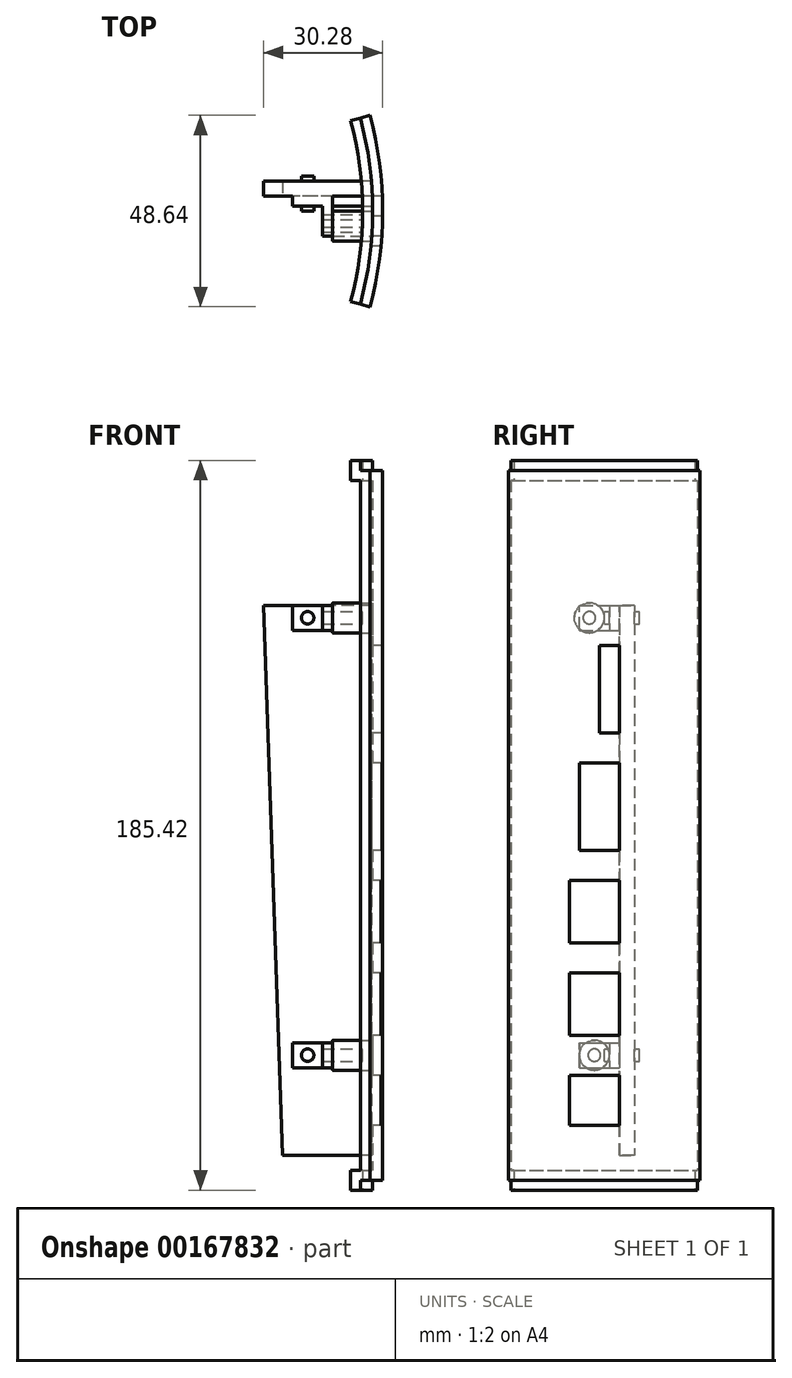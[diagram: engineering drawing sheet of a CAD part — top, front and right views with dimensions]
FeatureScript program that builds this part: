
annotation { "Feature Type Name" : "Feature", "Feature Type Description" : "" }
export const myFeature = defineFeature(function(context is Context, id is Id, definition is map)
    precondition{}
    {
        {
            var Q0;
            Q0=qCreatedBy(makeId("Front.planeOp"),FACE);
            var sketch = newSketch(context, id + "F0", { "sketchPlane" : qUnion([Q0])});
            skLineSegment(sketch, "E0.bottom", {"start": v(0, 146.05) * mm, "end": v(-27.74, 146.05) * mm});
            skLineSegment(sketch, "E0.top", {"start": v(0, 6.35) * mm, "end": v(-22.86, 6.35) * mm});
            skLineSegment(sketch, "E0.left", {"start": v(0, 146.05) * mm, "end": v(0, 6.35) * mm});
            skPoint(sketch, "E0.middle", {"position": v(0, 0) * mm});
            skLineSegment(sketch, "E1.top", {"start": v(2.54, 113.67) * mm, "end": v(-22.86, 113.67) * mm});
            skLineSegment(sketch, "E1.left", {"start": v(2.54, 135.89) * mm, "end": v(2.54, 113.66) * mm});
            skLineSegment(sketch, "E1.right", {"start": v(-22.86, 135.89) * mm, "end": v(-22.86, 113.66) * mm});
            skLineSegment(sketch, "E2.bottom", {"start": v(2.54, 106.05) * mm, "end": v(-19.69, 106.05) * mm});
            skLineSegment(sketch, "E2.top", {"start": v(2.54, 83.82) * mm, "end": v(-19.69, 83.82) * mm});
            skLineSegment(sketch, "E2.left", {"start": v(2.54, 106.04) * mm, "end": v(2.54, 83.82) * mm});
            skLineSegment(sketch, "E2.right", {"start": v(-19.69, 106.04) * mm, "end": v(-19.69, 83.82) * mm});
            skLineSegment(sketch, "E3.bottom", {"start": v(2.54, 76.2) * mm, "end": v(-15.88, 76.2) * mm});
            skLineSegment(sketch, "E3.top", {"start": v(2.54, 60.32) * mm, "end": v(-15.88, 60.32) * mm});
            skLineSegment(sketch, "E3.left", {"start": v(2.54, 76.2) * mm, "end": v(2.54, 60.32) * mm});
            skLineSegment(sketch, "E3.right", {"start": v(-15.88, 76.2) * mm, "end": v(-15.88, 60.32) * mm});
            skLineSegment(sketch, "E4.bottom", {"start": v(2.54, 52.7) * mm, "end": v(-13.34, 52.7) * mm});
            skLineSegment(sketch, "E4.top", {"start": v(2.54, 36.83) * mm, "end": v(-13.34, 36.83) * mm});
            skLineSegment(sketch, "E4.left", {"start": v(2.54, 52.7) * mm, "end": v(2.54, 36.83) * mm});
            skLineSegment(sketch, "E4.right", {"start": v(-13.34, 52.7) * mm, "end": v(-13.34, 36.83) * mm});
            skLineSegment(sketch, "E5.bottom", {"start": v(2.54, 26.67) * mm, "end": v(-16.51, 26.67) * mm});
            skLineSegment(sketch, "E5.top", {"start": v(2.54, 13.97) * mm, "end": v(-16.51, 13.97) * mm});
            skLineSegment(sketch, "E5.left", {"start": v(2.54, 26.67) * mm, "end": v(2.54, 13.97) * mm});
            skLineSegment(sketch, "E5.right", {"start": v(-16.51, 26.67) * mm, "end": v(-16.51, 13.97) * mm});
            skLineSegment(sketch, "E6", {"start": v(-22.86, 135.9) * mm, "end": v(2.54, 135.9) * mm});
            skLineSegment(sketch, "E7", {"start": v(-22.86, 6.35) * mm, "end": v(-27.74, 146.05) * mm});
            skLineSegment(sketch, "E8.bottom", {"start": v(-12.7, 139.7) * mm, "end": v(-20.32, 139.7) * mm});
            skLineSegment(sketch, "E8.top", {"start": v(-12.7, 146.05) * mm, "end": v(-22.86, 146.05) * mm});
            skLineSegment(sketch, "E8.left", {"start": v(-12.7, 139.7) * mm, "end": v(-12.7, 146.05) * mm});
            skLineSegment(sketch, "E9.bottom", {"start": v(-12.7, 28.57) * mm, "end": v(-20.32, 28.57) * mm});
            skLineSegment(sketch, "E9.top", {"start": v(-12.7, 34.92) * mm, "end": v(-20.32, 34.92) * mm});
            skLineSegment(sketch, "E9.left", {"start": v(-12.7, 28.57) * mm, "end": v(-12.7, 34.92) * mm});
            skLineSegment(sketch, "E10", {"start": v(-20.32, 34.92) * mm, "end": v(-20.32, 28.57) * mm});
            skLineSegment(sketch, "E11", {"start": v(-20.32, 146.05) * mm, "end": v(-20.32, 139.7) * mm});
            skCircle(sketch, "E12", {"center": v(-16.51, 31.75) * mm, "radius": 1.59 * mm});
            skCircle(sketch, "E13", {"center": v(-16.51, 142.87) * mm, "radius": 1.59 * mm});
            skPoint(sketch, "E14", {"position": v(0, 36.83) * mm});
            skPoint(sketch, "E15", {"position": v(0, 26.67) * mm});
            skPoint(sketch, "E16", {"position": v(0, 31.75) * mm});
            skLineSegment(sketch, "E17", {"start": v(0, 31.75) * mm, "end": v(-37.76, 31.75) * mm, "construction": true});
            skPoint(sketch, "E18", {"position": v(-12.7, 31.75) * mm});
            skPoint(sketch, "E19", {"position": v(-12.7, 142.87) * mm});
            skLineSegment(sketch, "E20", {"start": v(-2.37, 142.87) * mm, "end": v(-23.9, 142.87) * mm, "construction": true});
            skPoint(sketch, "E20.endSnap0", {"position": v(-22.86, 142.87) * mm});
            skLineSegment(sketch, "E21", {"start": v(-12.7, 139.7) * mm, "end": v(-10.16, 139.7) * mm});
            skLineSegment(sketch, "E22", {"start": v(-10.16, 139.7) * mm, "end": v(-10.16, 146.05) * mm});
            skLineSegment(sketch, "E23", {"start": v(-12.7, 34.92) * mm, "end": v(-10.16, 34.92) * mm});
            skLineSegment(sketch, "E24", {"start": v(-10.16, 34.92) * mm, "end": v(-10.16, 28.57) * mm});
            skLineSegment(sketch, "E25", {"start": v(-10.16, 28.57) * mm, "end": v(-12.7, 28.57) * mm});
            skSolve(sketch);
        }
        {
            var Q0;
            {var subQ5=sQuery(id+"F0.wireOp",EDGE,"E1.right");Q0=makeQuery(id+"F0.imprint","IMPRINT",FACE,{"disambiguationData":[TD([[makeQuery(id+"F0.imprint","IMPRINT",EDGE,{"derivedFrom":subQ5}),1.0]])]});}
            var Q1;
            {var subQ5=sQuery(id+"F0.wireOp",EDGE,"E4.right");Q1=makeQuery(id+"F0.imprint","IMPRINT",FACE,{"disambiguationData":[TD([[makeQuery(id+"F0.imprint","IMPRINT",EDGE,{"derivedFrom":subQ5}),1.0]])]});}
            var Q2;
            {var subQ5=sQuery(id+"F0.wireOp",EDGE,"E5.right");Q2=makeQuery(id+"F0.imprint","IMPRINT",FACE,{"disambiguationData":[TD([[makeQuery(id+"F0.imprint","IMPRINT",EDGE,{"derivedFrom":subQ5}),1.0]])]});}
            var Q3;
            {var subQ5=sQuery(id+"F0.wireOp",EDGE,"E2.right");Q3=makeQuery(id+"F0.imprint","IMPRINT",FACE,{"disambiguationData":[TD([[makeQuery(id+"F0.imprint","IMPRINT",EDGE,{"derivedFrom":subQ5}),1.0]])]});}
            var Q4;
            {var subQ5=sQuery(id+"F0.wireOp",EDGE,"E3.right");Q4=makeQuery(id+"F0.imprint","IMPRINT",FACE,{"disambiguationData":[TD([[makeQuery(id+"F0.imprint","IMPRINT",EDGE,{"derivedFrom":subQ5}),1.0]])]});}
            var Q5;
            {var subQ23=sQuery(id+"F0.wireOp",EDGE,"E0.bottom");Q5=makeQuery(id+"F0.imprint","IMPRINT",FACE,{"disambiguationData":[TD([[makeQuery(id+"F0.imprint","IMPRINT",EDGE,{"derivedFrom":subQ23}),1.0]])]});}
            var Q6;
            {var subQ5=sQuery(id+"F0.wireOp",EDGE,"E8.left");Q6=makeQuery(id+"F0.imprint","IMPRINT",FACE,{"disambiguationData":[TD([[makeQuery(id+"F0.imprint","IMPRINT",EDGE,{"derivedFrom":subQ5}),1.0]])]});}
            var Q7;
            {var subQ5=sQuery(id+"F0.wireOp",EDGE,"E9.left");Q7=makeQuery(id+"F0.imprint","IMPRINT",FACE,{"disambiguationData":[TD([[makeQuery(id+"F0.imprint","IMPRINT",EDGE,{"derivedFrom":subQ5}),1.0]])]});}
            var Q8;
            Q8=makeQuery(id+"F0.imprint","IMPRINT",FACE,{"disambiguationData":[TD([[makeQuery(id+"F0.imprint","IMPRINT",EDGE,{"derivedFrom":sQuery(id+"F0.wireOp",EDGE,"E12")}),1.0]])]});
            var Q9;
            Q9=makeQuery(id+"F0.imprint","IMPRINT",FACE,{"disambiguationData":[TD([[makeQuery(id+"F0.imprint","IMPRINT",EDGE,{"derivedFrom":sQuery(id+"F0.wireOp",EDGE,"E13")}),1.0]])]});
            var Q10;
            {var subQ0=sQuery(id+"F0.wireOp",EDGE,"E9.right");Q10=makeQuery(id+"F0.imprint","IMPRINT",FACE,{"disambiguationData":[TD([[makeQuery(id+"F0.imprint","IMPRINT",EDGE,{"derivedFrom":subQ0}),-1.0]])]});}
            var Q11;
            {var subQ0=sQuery(id+"F0.wireOp",EDGE,"E8.right");Q11=makeQuery(id+"F0.imprint","IMPRINT",FACE,{"disambiguationData":[TD([[makeQuery(id+"F0.imprint","IMPRINT",EDGE,{"derivedFrom":subQ0}),-1.0]])]});}
            var Q12;
            Q12=makeQuery(id+"F0.imprint","IMPRINT",FACE,{"disambiguationData":[TD([[makeQuery(id+"F0.imprint","IMPRINT",EDGE,{"derivedFrom":sQuery(id+"F0.wireOp",EDGE,"E9.left")}),-1.0]])]});
            var Q13;
            {var subQ0=sQuery(id+"F0.wireOp",EDGE,"E8.left");Q13=makeQuery(id+"F0.imprint","IMPRINT",FACE,{"disambiguationData":[TD([[makeQuery(id+"F0.imprint","IMPRINT",EDGE,{"derivedFrom":subQ0}),-1.0]])]});}
            extrude(context, id + "F1", {"entities" : qUnion([Q0, Q1, Q2, Q3, Q4, Q5, Q6, Q7, Q8, Q9, Q10, Q11, Q12, Q13]), "oppositeDirection" : true, "depth" : 3.8 * mm});
        }
        {
            var Q0;
            {var subQ5=sQuery(id+"F0.wireOp",EDGE,"E1.right");Q0=makeQuery(id+"F0.imprint","IMPRINT",FACE,{"disambiguationData":[TD([[makeQuery(id+"F0.imprint","IMPRINT",EDGE,{"derivedFrom":subQ5}),1.0]])]});}
            var Q1;
            {var subQ5=sQuery(id+"F0.wireOp",EDGE,"E1.left");Q1=makeQuery(id+"F0.imprint","IMPRINT",FACE,{"disambiguationData":[TD([[makeQuery(id+"F0.imprint","IMPRINT",EDGE,{"derivedFrom":subQ5}),-1.0]])]});}
            extrude(context, id + "F2", {"entities" : qUnion([Q0, Q1]), "operationType" : NewBodyOperationType.ADD, "depth" : 5.08 * mm});
        }
        {
            var Q0;
            Q0=makeQuery(id+"F0.imprint","IMPRINT",FACE,{"disambiguationData":[TD([[makeQuery(id+"F0.imprint","IMPRINT",EDGE,{"derivedFrom":sQuery(id+"F0.wireOp",EDGE,"E2.bottom")}),1.0]])]});
            extrude(context, id + "F3", {"entities" : qUnion([Q0]), "operationType" : NewBodyOperationType.ADD, "depth" : 10.16 * mm});
        }
        {
            var Q0;
            Q0=makeQuery(id+"F0.imprint","IMPRINT",FACE,{"disambiguationData":[TD([[makeQuery(id+"F0.imprint","IMPRINT",EDGE,{"derivedFrom":sQuery(id+"F0.wireOp",EDGE,"E3.bottom")}),1.0]])]});
            var Q1;
            Q1=makeQuery(id+"F0.imprint","IMPRINT",FACE,{"disambiguationData":[TD([[makeQuery(id+"F0.imprint","IMPRINT",EDGE,{"derivedFrom":sQuery(id+"F0.wireOp",EDGE,"E4.bottom")}),1.0]])]});
            var Q2;
            Q2=makeQuery(id+"F0.imprint","IMPRINT",FACE,{"disambiguationData":[TD([[makeQuery(id+"F0.imprint","IMPRINT",EDGE,{"derivedFrom":sQuery(id+"F0.wireOp",EDGE,"E5.bottom")}),1.0]])]});
            extrude(context, id + "F4", {"entities" : qUnion([Q0, Q1, Q2]), "operationType" : NewBodyOperationType.ADD, "depth" : 12.7 * mm});
        }
        {
            var Q0;
            Q0=makeQuery(id+"F4.opExtrude","SWEPT_FACE",FACE,{"disambiguationData":[OSD([sQuery(id+"F0.wireOp",EDGE,"E5.left")])]});
            var sketch = newSketch(context, id + "F5", { "sketchPlane" : qUnion([Q0])});
            skLineSegment(sketch, "E26.bottom", {"start": v(-10.58, 39.32) * mm, "end": v(-2.21, 39.32) * mm});
            skLineSegment(sketch, "E26.top", {"start": v(-10.58, 50.16) * mm, "end": v(-2.21, 50.16) * mm});
            skLineSegment(sketch, "E26.left", {"start": v(-10.58, 39.32) * mm, "end": v(-10.58, 50.16) * mm});
            skLineSegment(sketch, "E26.right", {"start": v(-2.21, 39.32) * mm, "end": v(-2.21, 50.16) * mm});
            skLineSegment(sketch, "E27.bottom", {"start": v(-8.75, 62.7) * mm, "end": v(-3.36, 62.7) * mm});
            skLineSegment(sketch, "E27.top", {"start": v(-8.75, 73.66) * mm, "end": v(-3.36, 73.66) * mm});
            skLineSegment(sketch, "E27.left", {"start": v(-8.75, 62.7) * mm, "end": v(-8.75, 73.66) * mm});
            skLineSegment(sketch, "E27.right", {"start": v(-3.36, 62.7) * mm, "end": v(-3.36, 73.66) * mm});
            skLineSegment(sketch, "E28.bottom", {"start": v(-6.74, 86.68) * mm, "end": v(-4.13, 86.68) * mm});
            skLineSegment(sketch, "E28.top", {"start": v(-6.74, 103.5) * mm, "end": v(-4.13, 103.5) * mm});
            skLineSegment(sketch, "E28.left", {"start": v(-6.74, 86.68) * mm, "end": v(-6.74, 103.5) * mm});
            skLineSegment(sketch, "E28.right", {"start": v(-4.13, 86.68) * mm, "end": v(-4.13, 103.5) * mm});
            skLineSegment(sketch, "E29.bottom", {"start": v(-2.9, 115.48) * mm, "end": v(-1.76, 115.48) * mm});
            skLineSegment(sketch, "E29.top", {"start": v(-2.9, 133.35) * mm, "end": v(-1.76, 133.35) * mm});
            skLineSegment(sketch, "E29.left", {"start": v(-2.9, 115.48) * mm, "end": v(-2.9, 133.35) * mm});
            skLineSegment(sketch, "E29.right", {"start": v(-1.76, 115.48) * mm, "end": v(-1.76, 133.35) * mm});
            skCircle(sketch, "E30", {"center": v(-6.52, 20.46) * mm, "radius": 4.3 * mm});
            skLineSegment(sketch, "E31.0.0", {"start": v(0, 113.67) * mm, "end": v(0, 135.89) * mm});
            skLineSegment(sketch, "E31.0.1", {"start": v(0, 135.89) * mm, "end": v(-5.08, 135.89) * mm});
            skLineSegment(sketch, "E31.0.2", {"start": v(-5.08, 135.89) * mm, "end": v(-5.08, 113.67) * mm});
            skLineSegment(sketch, "E31.0.3", {"start": v(-5.08, 113.67) * mm, "end": v(0, 113.67) * mm});
            skLineSegment(sketch, "E32.0.0", {"start": v(0, 83.82) * mm, "end": v(0, 106.05) * mm});
            skLineSegment(sketch, "E32.0.1", {"start": v(0, 106.05) * mm, "end": v(-10.16, 106.05) * mm});
            skLineSegment(sketch, "E32.0.2", {"start": v(-10.16, 106.05) * mm, "end": v(-10.16, 83.82) * mm});
            skLineSegment(sketch, "E32.0.3", {"start": v(-10.16, 83.82) * mm, "end": v(0, 83.82) * mm});
            skLineSegment(sketch, "E33.0.0", {"start": v(0, 60.32) * mm, "end": v(0, 76.2) * mm});
            skLineSegment(sketch, "E33.0.1", {"start": v(0, 76.2) * mm, "end": v(-12.7, 76.2) * mm});
            skLineSegment(sketch, "E33.0.2", {"start": v(-12.7, 76.2) * mm, "end": v(-12.7, 60.32) * mm});
            skLineSegment(sketch, "E33.0.3", {"start": v(-12.7, 60.32) * mm, "end": v(0, 60.32) * mm});
            skLineSegment(sketch, "E34.0.0", {"start": v(0, 36.83) * mm, "end": v(0, 52.7) * mm});
            skLineSegment(sketch, "E34.0.1", {"start": v(0, 52.7) * mm, "end": v(-12.7, 52.7) * mm});
            skLineSegment(sketch, "E34.0.2", {"start": v(-12.7, 52.7) * mm, "end": v(-12.7, 36.83) * mm});
            skLineSegment(sketch, "E34.0.3", {"start": v(-12.7, 36.83) * mm, "end": v(0, 36.83) * mm});
            skLineSegment(sketch, "E35.0.0", {"start": v(0, 13.97) * mm, "end": v(0, 26.67) * mm});
            skLineSegment(sketch, "E35.0.1", {"start": v(0, 26.67) * mm, "end": v(-12.7, 26.67) * mm});
            skLineSegment(sketch, "E35.0.2", {"start": v(-12.7, 26.67) * mm, "end": v(-12.7, 13.97) * mm});
            skLineSegment(sketch, "E35.0.3", {"start": v(-12.7, 13.97) * mm, "end": v(0, 13.97) * mm});
            skSolve(sketch);
        }
        {
            var Q0;
            Q0=makeQuery(id+"F5.imprint","IMPRINT",FACE,{"disambiguationData":[TD([[makeQuery(id+"F5.imprint","IMPRINT",EDGE,{"derivedFrom":sQuery(id+"F5.wireOp",EDGE,"QsPSDZzv-uLEy-goyq-KVDh-X1oqXHNKHxUB.bottom")}),1.0]])]});
            var Q1;
            Q1=makeQuery(id+"F5.imprint","IMPRINT",FACE,{"disambiguationData":[TD([[makeQuery(id+"F5.imprint","IMPRINT",EDGE,{"derivedFrom":sQuery(id+"F5.wireOp",EDGE,"E26.bottom")}),1.0]])]});
            var Q2;
            Q2=makeQuery(id+"F5.imprint","IMPRINT",FACE,{"disambiguationData":[TD([[makeQuery(id+"F5.imprint","IMPRINT",EDGE,{"derivedFrom":sQuery(id+"F5.wireOp",EDGE,"E27.bottom")}),1.0]])]});
            var Q3;
            Q3=makeQuery(id+"F5.imprint","IMPRINT",FACE,{"disambiguationData":[TD([[makeQuery(id+"F5.imprint","IMPRINT",EDGE,{"derivedFrom":sQuery(id+"F5.wireOp",EDGE,"E28.bottom")}),1.0]])]});
            var Q4;
            Q4=makeQuery(id+"F5.imprint","IMPRINT",FACE,{"disambiguationData":[TD([[makeQuery(id+"F5.imprint","IMPRINT",EDGE,{"derivedFrom":sQuery(id+"F5.wireOp",EDGE,"E29.bottom")}),1.0]])]});
            var Q5;
            Q5=makeQuery(id+"F5.imprint","IMPRINT",FACE,{"disambiguationData":[TD([[makeQuery(id+"F5.imprint","IMPRINT",EDGE,{"derivedFrom":sQuery(id+"F5.wireOp",EDGE,"E30")}),1.0]])]});
            extrude(context, id + "F6", {"entities" : qUnion([Q0, Q1, Q2, Q3, Q4, Q5]), "operationType" : NewBodyOperationType.REMOVE, "oppositeDirection" : true, "depth" : 12.7 * mm});
        }
        {
            var Q0;
            {var subQ5=sQuery(id+"F0.wireOp",EDGE,"E8.left");Q0=makeQuery(id+"F0.imprint","IMPRINT",FACE,{"disambiguationData":[TD([[makeQuery(id+"F0.imprint","IMPRINT",EDGE,{"derivedFrom":subQ5}),1.0]])]});}
            var Q1;
            {var subQ5=sQuery(id+"F0.wireOp",EDGE,"E11");Q1=makeQuery(id+"F0.imprint","IMPRINT",FACE,{"disambiguationData":[TD([[makeQuery(id+"F0.imprint","IMPRINT",EDGE,{"derivedFrom":subQ5}),1.0]])]});}
            var Q2;
            {var subQ0=sQuery(id+"F0.wireOp",EDGE,"E8.right");Q2=makeQuery(id+"F0.imprint","IMPRINT",FACE,{"disambiguationData":[TD([[makeQuery(id+"F0.imprint","IMPRINT",EDGE,{"derivedFrom":subQ0}),-1.0]])]});}
            var Q3;
            {var subQ5=sQuery(id+"F0.wireOp",EDGE,"E9.left");Q3=makeQuery(id+"F0.imprint","IMPRINT",FACE,{"disambiguationData":[TD([[makeQuery(id+"F0.imprint","IMPRINT",EDGE,{"derivedFrom":subQ5}),1.0]])]});}
            var Q4;
            {var subQ5=sQuery(id+"F0.wireOp",EDGE,"E10");Q4=makeQuery(id+"F0.imprint","IMPRINT",FACE,{"disambiguationData":[TD([[makeQuery(id+"F0.imprint","IMPRINT",EDGE,{"derivedFrom":subQ5}),1.0]])]});}
            var Q5;
            {var subQ0=sQuery(id+"F0.wireOp",EDGE,"E9.right");Q5=makeQuery(id+"F0.imprint","IMPRINT",FACE,{"disambiguationData":[TD([[makeQuery(id+"F0.imprint","IMPRINT",EDGE,{"derivedFrom":subQ0}),-1.0]])]});}
            extrude(context, id + "F7", {"entities" : qUnion([Q0, Q1, Q2, Q3, Q4, Q5]), "operationType" : NewBodyOperationType.ADD, "depth" : 2.54 * mm});
        }
        {
            var Q0;
            {var subQ0=sQuery(id+"F0.wireOp",EDGE,"E8.left");Q0=makeQuery(id+"F0.imprint","IMPRINT",FACE,{"disambiguationData":[TD([[makeQuery(id+"F0.imprint","IMPRINT",EDGE,{"derivedFrom":subQ0}),-1.0]])]});}
            var Q1;
            Q1=makeQuery(id+"F0.imprint","IMPRINT",FACE,{"disambiguationData":[TD([[makeQuery(id+"F0.imprint","IMPRINT",EDGE,{"derivedFrom":sQuery(id+"F0.wireOp",EDGE,"E9.left")}),-1.0]])]});
            extrude(context, id + "F8", {"entities" : qUnion([Q0, Q1]), "operationType" : NewBodyOperationType.ADD, "depth" : 10.16 * mm});
        }
        {
            var Q0;
            Q0=makeQuery(id+"F0.imprint","IMPRINT",FACE,{"disambiguationData":[TD([[makeQuery(id+"F0.imprint","IMPRINT",EDGE,{"derivedFrom":sQuery(id+"F0.wireOp",EDGE,"E13")}),1.0]])]});
            var Q1;
            Q1=makeQuery(id+"F0.imprint","IMPRINT",FACE,{"disambiguationData":[TD([[makeQuery(id+"F0.imprint","IMPRINT",EDGE,{"derivedFrom":sQuery(id+"F0.wireOp",EDGE,"E12")}),1.0]])]});
            extrude(context, id + "F9", {"entities" : qUnion([Q0, Q1]), "operationType" : NewBodyOperationType.ADD, "depth" : 3.8 * mm, "hasSecondDirection" : true, "secondDirectionOppositeDirection" : true, "secondDirectionDepth" : 5.08 * mm});
        }
        {
            var Q0;
            Q0=qCreatedBy(makeId("Right.planeOp"),FACE);
            var sketch = newSketch(context, id + "F10", { "sketchPlane" : qUnion([Q0])});
            skLineSegment(sketch, "E36.0.0", {"start": v(0, 139.7) * mm, "end": v(0, 146.05) * mm});
            skLineSegment(sketch, "E36.0.1", {"start": v(-10.16, 139.7) * mm, "end": v(0, 139.7) * mm});
            skLineSegment(sketch, "E36.0.2", {"start": v(-10.16, 146.05) * mm, "end": v(-10.16, 139.7) * mm});
            skLineSegment(sketch, "E36.0.3", {"start": v(0, 146.05) * mm, "end": v(-10.16, 146.05) * mm});
            skLineSegment(sketch, "E37.0.0", {"start": v(0, 28.57) * mm, "end": v(0, 34.92) * mm});
            skLineSegment(sketch, "E37.0.1", {"start": v(-10.16, 28.57) * mm, "end": v(0, 28.57) * mm});
            skLineSegment(sketch, "E37.0.2", {"start": v(-10.16, 34.92) * mm, "end": v(-10.16, 28.57) * mm});
            skLineSegment(sketch, "E37.0.3", {"start": v(0, 34.92) * mm, "end": v(-10.16, 34.92) * mm});
            skPoint(sketch, "E38", {"position": v(-10.16, 142.87) * mm});
            skLineSegment(sketch, "E39", {"start": v(0, 142.87) * mm, "end": v(-10.16, 142.87) * mm, "construction": true});
            skCircle(sketch, "E40", {"center": v(-7.62, 142.87) * mm, "radius": 1.59 * mm});
            skCircle(sketch, "E41", {"center": v(-7.62, 142.87) * mm, "radius": 3.81 * mm});
            skPoint(sketch, "E42", {"position": v(-10.16, 31.75) * mm});
            skLineSegment(sketch, "E43", {"start": v(0, 31.75) * mm, "end": v(-10.16, 31.75) * mm, "construction": true});
            skCircle(sketch, "E44", {"center": v(-6.35, 31.75) * mm, "radius": 1.59 * mm});
            skCircle(sketch, "E45", {"center": v(-6.35, 31.75) * mm, "radius": 3.81 * mm});
            skSolve(sketch);
        }
        {
            var Q0;
            Q0=makeQuery(id+"F10.imprint","IMPRINT",FACE,{"disambiguationData":[TD([[makeQuery(id+"F10.imprint","IMPRINT",EDGE,{"derivedFrom":sQuery(id+"F10.wireOp",EDGE,"mAwodLHo-5CJ7-BU8g-Eq2X-gMBFYanYIdpS")}),1.0]])]});
            var Q1;
            {var subQ0=sQuery(id+"F10.wireOp",EDGE,"BFzIXqao-JbxE-Ypqr-w9Nd-hP7NoaJlb3yi");var subQ1=sQuery(id+"F10.wireOp",EDGE,"04AyWxKv-bo47-RNZc-UAjW-Hn0S6AFtiVpr");var subQ2=makeQuery(id+"F10.imprint","INTERSECT",VERTEX,{"disambiguationData":[OD(0.0)],"derivedFrom":[subQ1,subQ0]});Q1=makeQuery(id+"F10.imprint","IMPRINT",FACE,{"disambiguationData":[TD([[makeQuery(id+"F10.imprint","IMPRINT",EDGE,{"disambiguationData":[TD([[subQ2,1.0]])],"derivedFrom":subQ1}),1.0]])]});}
            var Q2;
            {var subQ0=sQuery(id+"F10.wireOp",EDGE,"9as04cPz-zgJ7-VkpZ-YAaS-p6B9O8Tkpz6i");var subQ1=sQuery(id+"F10.wireOp",EDGE,"04AyWxKv-bo47-RNZc-UAjW-Hn0S6AFtiVpr");var subQ2=makeQuery(id+"F10.imprint","INTERSECT",VERTEX,{"disambiguationData":[OD(0.0)],"derivedFrom":[subQ1,subQ0]});Q2=makeQuery(id+"F10.imprint","IMPRINT",FACE,{"disambiguationData":[TD([[makeQuery(id+"F10.imprint","IMPRINT",EDGE,{"disambiguationData":[TD([[subQ2,1.0]])],"derivedFrom":subQ1}),1.0]])]});}
            var Q3;
            {var subQ0=sQuery(id+"F10.wireOp",EDGE,"9as04cPz-zgJ7-VkpZ-YAaS-p6B9O8Tkpz6i");var subQ1=sQuery(id+"F10.wireOp",EDGE,"04AyWxKv-bo47-RNZc-UAjW-Hn0S6AFtiVpr");var subQ2=makeQuery(id+"F10.imprint","INTERSECT",VERTEX,{"disambiguationData":[OD(0.0)],"derivedFrom":[subQ1,subQ0]});Q3=makeQuery(id+"F10.imprint","IMPRINT",FACE,{"disambiguationData":[TD([[makeQuery(id+"F10.imprint","IMPRINT",EDGE,{"disambiguationData":[TD([[subQ2,-1.0]])],"derivedFrom":subQ1}),1.0]])]});}
            var Q4;
            {var subQ0=sQuery(id+"F10.wireOp",EDGE,"BFzIXqao-JbxE-Ypqr-w9Nd-hP7NoaJlb3yi");var subQ1=sQuery(id+"F10.wireOp",EDGE,"04AyWxKv-bo47-RNZc-UAjW-Hn0S6AFtiVpr");var subQ2=makeQuery(id+"F10.imprint","INTERSECT",VERTEX,{"disambiguationData":[OD(1.0)],"derivedFrom":[subQ1,subQ0]});Q4=makeQuery(id+"F10.imprint","IMPRINT",FACE,{"disambiguationData":[TD([[makeQuery(id+"F10.imprint","IMPRINT",EDGE,{"disambiguationData":[TD([[subQ2,-1.0]])],"derivedFrom":subQ1}),1.0]])]});}
            var Q5;
            Q5=makeQuery(id+"F10.imprint","IMPRINT",FACE,{"disambiguationData":[TD([[makeQuery(id+"F10.imprint","IMPRINT",EDGE,{"derivedFrom":sQuery(id+"F10.wireOp",EDGE,"E44")}),1.0]])]});
            var Q6;
            Q6=makeQuery(id+"F10.imprint","IMPRINT",FACE,{"disambiguationData":[TD([[makeQuery(id+"F10.imprint","IMPRINT",EDGE,{"derivedFrom":sQuery(id+"F10.wireOp",EDGE,"E40")}),1.0]])]});
            extrude(context, id + "F11", {"entities" : qUnion([Q0, Q1, Q2, Q3, Q4, Q5, Q6]), "operationType" : NewBodyOperationType.REMOVE, "oppositeDirection" : true, "depth" : 25.4 * mm});
        }
        {
            var Q0;
            Q0=qCreatedBy(makeId("Top.planeOp"),FACE);
            var sketch = newSketch(context, id + "F12", { "sketchPlane" : qUnion([Q0])});
            skCircle(sketch, "E46", {"center": v(-91.44, -3.81) * mm, "radius": 93.98 * mm});
            skCircle(sketch, "E47", {"center": v(-91.44, -3.81) * mm, "radius": 91.44 * mm});
            skCircle(sketch, "E48", {"center": v(-91.44, -3.81) * mm, "radius": 88.9 * mm});
            skLineSegment(sketch, "E49", {"start": v(-91.44, -3.81) * mm, "end": v(20.53, -3.81) * mm, "construction": true});
            skLineSegment(sketch, "E50", {"start": v(-91.44, -3.81) * mm, "end": v(-0.66, -28.13) * mm});
            skLineSegment(sketch, "E51.MirrorCS", {"start": v(-91.44, -3.81) * mm, "end": v(-0.66, 20.51) * mm});
            skPoint(sketch, "E52", {"position": v(0, -3.81) * mm});
            skSolve(sketch);
        }
        {
            var Q0;
            {var subQ0=sQuery(id+"F12.wireOp",EDGE,"E50");var subQ1=sQuery(id+"F12.wireOp",EDGE,"E46");var subQ2=makeQuery(id+"F12.imprint","INTERSECT",VERTEX,{"derivedFrom":[subQ1,subQ0]});Q0=makeQuery(id+"F12.imprint","IMPRINT",FACE,{"disambiguationData":[TD([[makeQuery(id+"F12.imprint","IMPRINT",EDGE,{"disambiguationData":[TD([[subQ2,-1.0]])],"derivedFrom":subQ1}),1.0]])]});}
            extrude(context, id + "F13", {"entities" : qUnion([Q0]), "depth" : 180.34 * mm});
        }
        {
            var Q0;
            Q0=makeQuery(id+"F5.imprint","IMPRINT",FACE,{"disambiguationData":[TD([[makeQuery(id+"F5.imprint","IMPRINT",EDGE,{"derivedFrom":sQuery(id+"F5.wireOp",EDGE,"E28.bottom")}),-1.0]])]});
            var Q1;
            Q1=makeQuery(id+"F5.imprint","IMPRINT",FACE,{"disambiguationData":[TD([[makeQuery(id+"F5.imprint","IMPRINT",EDGE,{"derivedFrom":sQuery(id+"F5.wireOp",EDGE,"E28.bottom")}),1.0]])]});
            var Q2;
            Q2=makeQuery(id+"F5.imprint","IMPRINT",FACE,{"disambiguationData":[TD([[makeQuery(id+"F5.imprint","IMPRINT",EDGE,{"derivedFrom":sQuery(id+"F5.wireOp",EDGE,"E29.bottom")}),-1.0]])]});
            var Q3;
            Q3=makeQuery(id+"F5.imprint","IMPRINT",FACE,{"disambiguationData":[TD([[makeQuery(id+"F5.imprint","IMPRINT",EDGE,{"derivedFrom":sQuery(id+"F5.wireOp",EDGE,"E29.bottom")}),1.0]])]});
            var Q4;
            Q4=makeQuery(id+"F5.imprint","IMPRINT",FACE,{"disambiguationData":[TD([[makeQuery(id+"F5.imprint","IMPRINT",EDGE,{"derivedFrom":sQuery(id+"F5.wireOp",EDGE,"E27.bottom")}),-1.0]])]});
            var Q5;
            Q5=makeQuery(id+"F5.imprint","IMPRINT",FACE,{"disambiguationData":[TD([[makeQuery(id+"F5.imprint","IMPRINT",EDGE,{"derivedFrom":sQuery(id+"F5.wireOp",EDGE,"E27.bottom")}),1.0]])]});
            var Q6;
            Q6=makeQuery(id+"F5.imprint","IMPRINT",FACE,{"disambiguationData":[TD([[makeQuery(id+"F5.imprint","IMPRINT",EDGE,{"derivedFrom":sQuery(id+"F5.wireOp",EDGE,"E26.bottom")}),-1.0]])]});
            var Q7;
            Q7=makeQuery(id+"F5.imprint","IMPRINT",FACE,{"disambiguationData":[TD([[makeQuery(id+"F5.imprint","IMPRINT",EDGE,{"derivedFrom":sQuery(id+"F5.wireOp",EDGE,"E26.bottom")}),1.0]])]});
            var Q8;
            Q8=makeQuery(id+"F5.imprint","IMPRINT",FACE,{"disambiguationData":[TD([[makeQuery(id+"F5.imprint","IMPRINT",EDGE,{"derivedFrom":sQuery(id+"F5.wireOp",EDGE,"E30")}),1.0]])]});
            var Q9;
            Q9=makeQuery(id+"F5.imprint","IMPRINT",FACE,{"disambiguationData":[TD([[makeQuery(id+"F5.imprint","IMPRINT",EDGE,{"derivedFrom":sQuery(id+"F5.wireOp",EDGE,"E30")}),-1.0]])]});
            extrude(context, id + "F14", {"entities" : qUnion([Q0, Q1, Q2, Q3, Q4, Q5, Q6, Q7, Q8, Q9]), "operationType" : NewBodyOperationType.REMOVE, "depth" : 25.4 * mm, "hasSecondDirection" : true, "secondDirectionOppositeDirection" : true, "secondDirectionDepth" : 25.4 * mm});
        }
        {
            var Q0;
            {var subQ0=sQuery(id+"F10.wireOp",EDGE,"E41");var subQ1=sQuery(id+"F10.wireOp",EDGE,"E36.0.1");var subQ2=makeQuery(id+"F10.imprint","INTERSECT",VERTEX,{"disambiguationData":[OD(0.0)],"derivedFrom":[subQ1,subQ0]});Q0=makeQuery(id+"F10.imprint","IMPRINT",FACE,{"disambiguationData":[TD([[makeQuery(id+"F10.imprint","IMPRINT",EDGE,{"disambiguationData":[TD([[subQ2,-1.0]])],"derivedFrom":subQ1}),-1.0]])]});}
            var Q1;
            Q1=makeQuery(id+"F10.imprint","IMPRINT",FACE,{"disambiguationData":[TD([[makeQuery(id+"F10.imprint","IMPRINT",EDGE,{"derivedFrom":sQuery(id+"F10.wireOp",EDGE,"E40")}),-1.0]])]});
            var Q2;
            Q2=makeQuery(id+"F10.imprint","IMPRINT",FACE,{"disambiguationData":[TD([[makeQuery(id+"F10.imprint","IMPRINT",EDGE,{"derivedFrom":sQuery(id+"F10.wireOp",EDGE,"E40")}),1.0]])]});
            var Q3;
            {var subQ0=sQuery(id+"F10.wireOp",EDGE,"E45");var subQ1=sQuery(id+"F10.wireOp",EDGE,"E37.0.1");var subQ2=makeQuery(id+"F10.imprint","INTERSECT",VERTEX,{"disambiguationData":[OD(0.0)],"derivedFrom":[subQ1,subQ0]});Q3=makeQuery(id+"F10.imprint","IMPRINT",FACE,{"disambiguationData":[TD([[makeQuery(id+"F10.imprint","IMPRINT",EDGE,{"disambiguationData":[TD([[subQ2,-1.0]])],"derivedFrom":subQ1}),-1.0]])]});}
            var Q4;
            Q4=makeQuery(id+"F10.imprint","IMPRINT",FACE,{"disambiguationData":[TD([[makeQuery(id+"F10.imprint","IMPRINT",EDGE,{"derivedFrom":sQuery(id+"F10.wireOp",EDGE,"E44")}),-1.0]])]});
            var Q5;
            {var subQ0=sQuery(id+"F10.wireOp",EDGE,"E45");var subQ1=sQuery(id+"F10.wireOp",EDGE,"E37.0.3");var subQ2=makeQuery(id+"F10.imprint","INTERSECT",VERTEX,{"disambiguationData":[OD(0.0)],"derivedFrom":[subQ1,subQ0]});Q5=makeQuery(id+"F10.imprint","IMPRINT",FACE,{"disambiguationData":[TD([[makeQuery(id+"F10.imprint","IMPRINT",EDGE,{"disambiguationData":[TD([[subQ2,-1.0]])],"derivedFrom":subQ1}),-1.0]])]});}
            var Q6;
            Q6=makeQuery(id+"F10.imprint","IMPRINT",FACE,{"disambiguationData":[TD([[makeQuery(id+"F10.imprint","IMPRINT",EDGE,{"derivedFrom":sQuery(id+"F10.wireOp",EDGE,"E44")}),1.0]])]});
            var Q7;
            {var subQ0=sQuery(id+"F10.wireOp",EDGE,"E41");var subQ1=sQuery(id+"F10.wireOp",EDGE,"E36.0.3");var subQ2=makeQuery(id+"F10.imprint","INTERSECT",VERTEX,{"disambiguationData":[OD(0.0)],"derivedFrom":[subQ1,subQ0]});Q7=makeQuery(id+"F10.imprint","IMPRINT",FACE,{"disambiguationData":[TD([[makeQuery(id+"F10.imprint","IMPRINT",EDGE,{"disambiguationData":[TD([[subQ2,-1.0]])],"derivedFrom":subQ1}),-1.0]])]});}
            var Q8;
            {var subQ0=sQuery(id+"F10.wireOp",EDGE,"E41");var subQ1=sQuery(id+"F10.wireOp",EDGE,"E36.0.2");var subQ2=makeQuery(id+"F10.imprint","INTERSECT",VERTEX,{"disambiguationData":[OD(0.0)],"derivedFrom":[subQ1,subQ0]});Q8=makeQuery(id+"F10.imprint","IMPRINT",FACE,{"disambiguationData":[TD([[makeQuery(id+"F10.imprint","IMPRINT",EDGE,{"disambiguationData":[TD([[subQ2,-1.0]])],"derivedFrom":subQ1}),-1.0]])]});}
            var Q9;
            Q9=makeQuery(id+"F8.opExtrude","SWEPT_FACE",FACE,{"disambiguationData":[OSD([sQuery(id+"F0.wireOp",EDGE,"E24")])]});
            var Q10;
            Q10=makeQuery(id+"F1.opExtrude","SWEPT_BODY",BODY,{"disambiguationData":[OSD([sQuery(id+"F0.wireOp",EDGE,"E0.bottom"),sQuery(id+"F0.wireOp",EDGE,"E0.top"),sQuery(id+"F0.wireOp",EDGE,"E0.left"),sQuery(id+"F0.wireOp",EDGE,"E7"),sQuery(id+"F0.wireOp",EDGE,"E8.top")])]});
            extrude(context, id + "F15", {"entities" : qUnion([Q0, Q1, Q2, Q3, Q4, Q5, Q6, Q7, Q8]), "operationType" : NewBodyOperationType.ADD, "endBound" : BoundingType.UP_TO_SURFACE, "oppositeDirection" : true, "endBoundEntityFace" : qUnion([Q9]), "endBoundEntityBody" : qUnion([Q10]), "depth" : 25.4 * mm, "hasSecondDirection" : true, "secondDirectionBound" : BoundingType.UP_TO_NEXT, "secondDirectionOppositeDirection" : false, "secondDirectionDepth" : 25.4 * mm});
        }
        {
            var Q0;
            Q0=makeQuery(id+"F10.imprint","IMPRINT",FACE,{"disambiguationData":[TD([[makeQuery(id+"F10.imprint","IMPRINT",EDGE,{"derivedFrom":sQuery(id+"F10.wireOp",EDGE,"E40")}),1.0]])]});
            var Q1;
            Q1=makeQuery(id+"F10.imprint","IMPRINT",FACE,{"disambiguationData":[TD([[makeQuery(id+"F10.imprint","IMPRINT",EDGE,{"derivedFrom":sQuery(id+"F10.wireOp",EDGE,"E44")}),1.0]])]});
            extrude(context, id + "F16", {"entities" : qUnion([Q0, Q1]), "operationType" : NewBodyOperationType.REMOVE, "oppositeDirection" : true, "depth" : 25.4 * mm, "hasSecondDirection" : true, "secondDirectionOppositeDirection" : true, "secondDirectionDepth" : 2.54 * mm});
        }
        {
            var Q0;
            {var subQ0=sQuery(id+"F12.wireOp",EDGE,"E50");var subQ1=sQuery(id+"F12.wireOp",EDGE,"E47");var subQ2=makeQuery(id+"F12.imprint","INTERSECT",VERTEX,{"derivedFrom":[subQ1,subQ0]});Q0=makeQuery(id+"F12.imprint","IMPRINT",FACE,{"disambiguationData":[TD([[makeQuery(id+"F12.imprint","IMPRINT",EDGE,{"disambiguationData":[TD([[subQ2,-1.0]])],"derivedFrom":subQ1}),1.0]])]});}
            extrude(context, id + "F17", {"entities" : qUnion([Q0]), "operationType" : NewBodyOperationType.ADD, "depth" : 182.88 * mm, "hasSecondDirection" : true, "secondDirectionOppositeDirection" : false, "secondDirectionDepth" : 177.8 * mm});
        }
        {
            var Q0;
            {var subQ0=sQuery(id+"F12.wireOp",EDGE,"E50");var subQ1=sQuery(id+"F12.wireOp",EDGE,"E47");var subQ2=makeQuery(id+"F12.imprint","INTERSECT",VERTEX,{"derivedFrom":[subQ1,subQ0]});Q0=makeQuery(id+"F12.imprint","IMPRINT",FACE,{"disambiguationData":[TD([[makeQuery(id+"F12.imprint","IMPRINT",EDGE,{"disambiguationData":[TD([[subQ2,-1.0]])],"derivedFrom":subQ1}),1.0]])]});}
            extrude(context, id + "F18", {"entities" : qUnion([Q0]), "operationType" : NewBodyOperationType.ADD, "depth" : 2.54 * mm, "hasSecondDirection" : true, "secondDirectionOppositeDirection" : true, "secondDirectionDepth" : 2.54 * mm});
        }
    });
